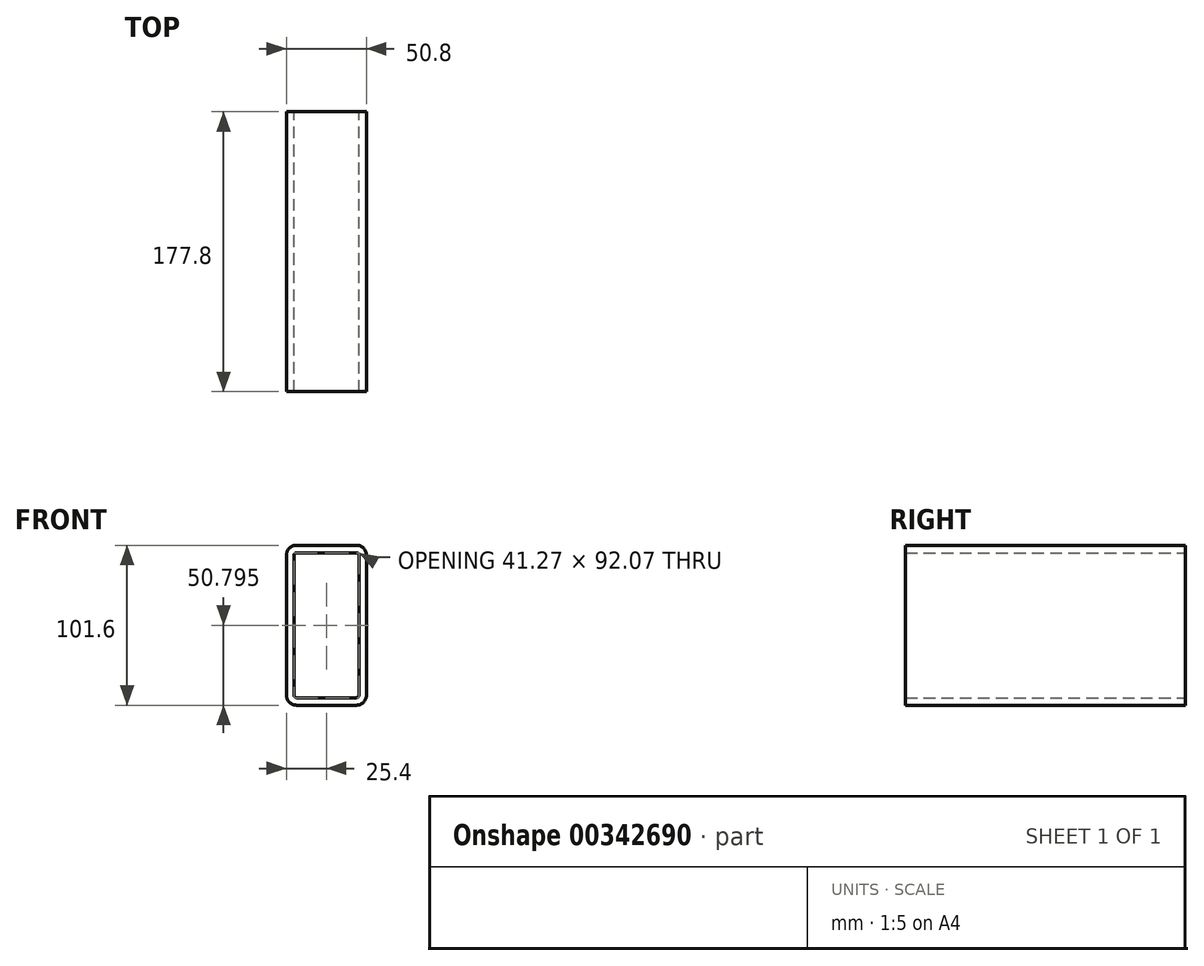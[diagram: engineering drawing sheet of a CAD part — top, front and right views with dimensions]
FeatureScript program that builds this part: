
annotation { "Feature Type Name" : "Feature", "Feature Type Description" : "" }
export const myFeature = defineFeature(function(context is Context, id is Id, definition is map)
    precondition{}
    {
        {
            var Q0;
            Q0=qCreatedBy(makeId("Front.planeOp"),FACE);
            var sketch = newSketch(context, id + "F0", { "sketchPlane" : qUnion([Q0])});
            skLineSegment(sketch, "E0.bottom", {"start": v(-19.05, 50.8) * mm, "end": v(19.05, 50.8) * mm});
            skLineSegment(sketch, "E0.top", {"start": v(-19.05, -50.8) * mm, "end": v(19.05, -50.8) * mm});
            skLineSegment(sketch, "E0.left", {"start": v(-25.4, 44.45) * mm, "end": v(-25.4, -44.45) * mm});
            skLineSegment(sketch, "E0.right", {"start": v(25.4, 44.45) * mm, "end": v(25.4, -44.45) * mm});
            skPoint(sketch, "E0.middle", {"position": v(0, 0) * mm});
            skPoint(sketch, "E1.visualSharp", {"position": v(-25.4, 50.8) * mm});
            skArc(sketch, "E1.filletArc", {"start": v(-19.05, 50.8) * mm, "mid": v(-23.54, 48.94) * mm, "end": v(-25.4, 44.45) * mm});
            skPoint(sketch, "E2.visualSharp", {"position": v(25.4, 50.8) * mm});
            skArc(sketch, "E2.filletArc", {"start": v(25.4, 44.45) * mm, "mid": v(23.54, 48.94) * mm, "end": v(19.05, 50.8) * mm});
            skPoint(sketch, "E3.visualSharp", {"position": v(25.4, -50.8) * mm});
            skArc(sketch, "E3.filletArc", {"start": v(19.05, -50.8) * mm, "mid": v(23.54, -48.94) * mm, "end": v(25.4, -44.45) * mm});
            skPoint(sketch, "E4.visualSharp", {"position": v(-25.4, -50.8) * mm});
            skArc(sketch, "E4.filletArc", {"start": v(-25.4, -44.45) * mm, "mid": v(-23.54, -48.94) * mm, "end": v(-19.05, -50.8) * mm});
            skLineSegment(sketch, "E5.0", {"start": v(-19.05, 46.03) * mm, "end": v(19.05, 46.03) * mm});
            skLineSegment(sketch, "E5.1", {"start": v(-20.64, 44.44) * mm, "end": v(-20.64, -44.45) * mm});
            skLineSegment(sketch, "E5.2", {"start": v(-19.05, -46.04) * mm, "end": v(19.05, -46.04) * mm});
            skLineSegment(sketch, "E5.3", {"start": v(20.64, 44.44) * mm, "end": v(20.64, -44.45) * mm});
            skPoint(sketch, "E6.visualSharp", {"position": v(-20.64, 46.03) * mm});
            skArc(sketch, "E6.filletArc", {"start": v(-19.05, 46.03) * mm, "mid": v(-20.17, 45.56) * mm, "end": v(-20.64, 44.44) * mm});
            skPoint(sketch, "E7.visualSharp", {"position": v(20.64, 46.03) * mm});
            skArc(sketch, "E7.filletArc", {"start": v(20.64, 44.44) * mm, "mid": v(20.17, 45.56) * mm, "end": v(19.05, 46.03) * mm});
            skPoint(sketch, "E8.visualSharp", {"position": v(20.64, -46.04) * mm});
            skArc(sketch, "E8.filletArc", {"start": v(19.05, -46.04) * mm, "mid": v(20.17, -45.57) * mm, "end": v(20.64, -44.45) * mm});
            skPoint(sketch, "E9.visualSharp", {"position": v(-20.64, -46.04) * mm});
            skArc(sketch, "E9.filletArc", {"start": v(-20.64, -44.45) * mm, "mid": v(-20.17, -45.57) * mm, "end": v(-19.05, -46.04) * mm});
            skSolve(sketch);
        }
        {
            var Q0;
            Q0=makeQuery(id+"F0.imprint","IMPRINT",FACE,{"disambiguationData":[TD([[makeQuery(id+"F0.imprint","IMPRINT",EDGE,{"derivedFrom":sQuery(id+"F0.wireOp",EDGE,"E0.bottom")}),-1.0]])]});
            extrude(context, id + "F1", {"entities" : qUnion([Q0]), "depth" : 177.8 * mm});
        }
    });
